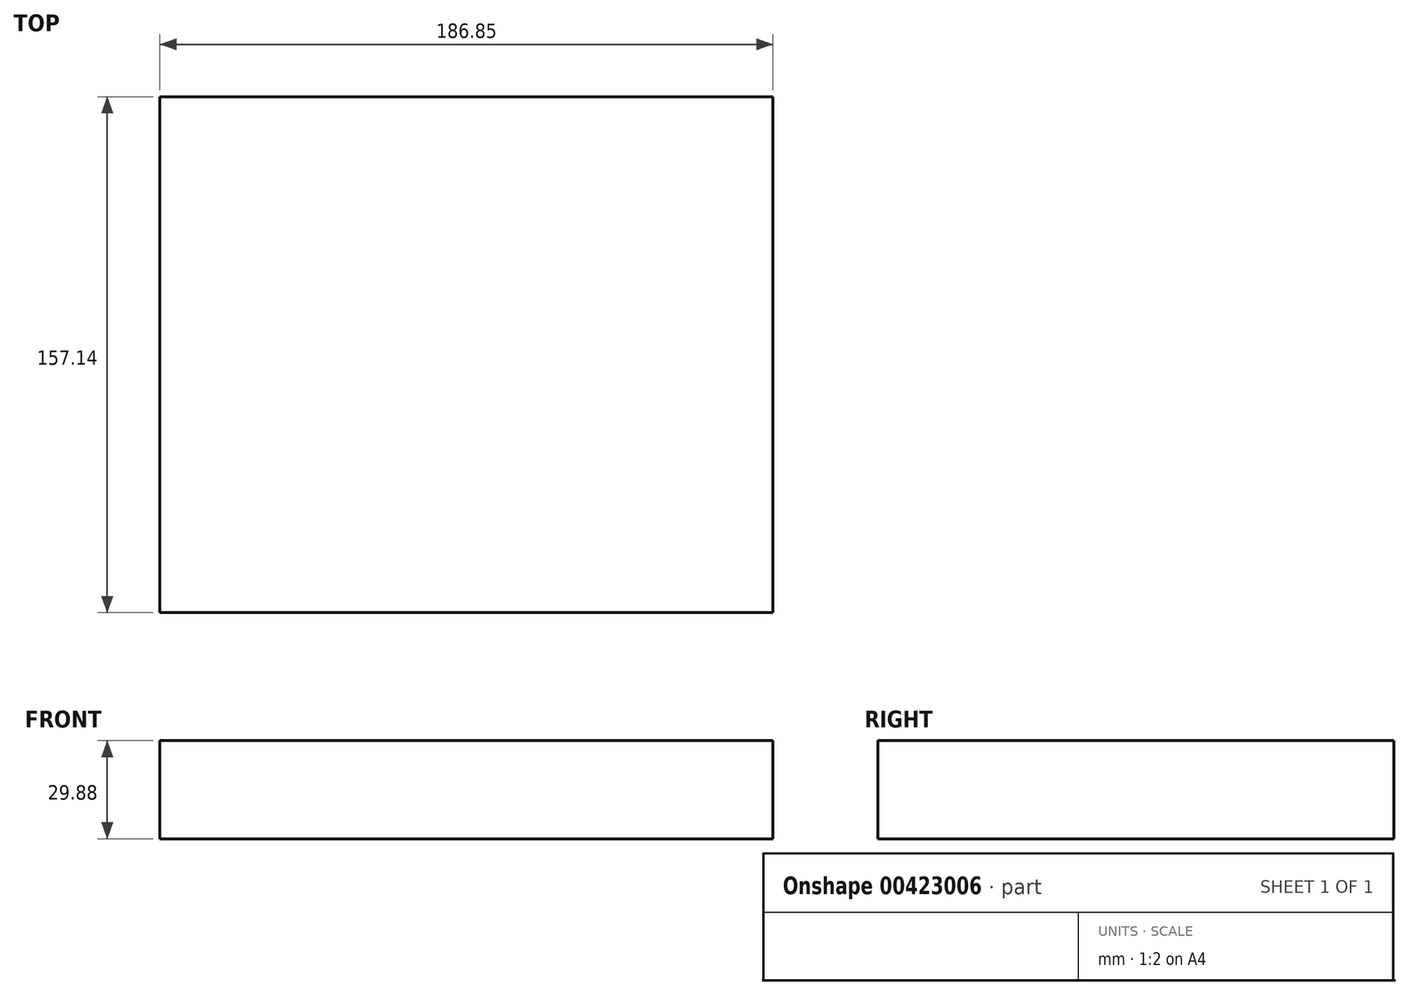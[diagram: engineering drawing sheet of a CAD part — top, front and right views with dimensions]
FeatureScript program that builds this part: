
annotation { "Feature Type Name" : "Feature", "Feature Type Description" : "" }
export const myFeature = defineFeature(function(context is Context, id is Id, definition is map)
    precondition{}
    {
        {
            var Q0;
            Q0=qCreatedBy(makeId("Front.planeOp"),FACE);
            var sketch = newSketch(context, id + "F0", { "sketchPlane" : qUnion([Q0])});
            skLineSegment(sketch, "E0.bottom", {"start": v(2281.78, 343.59) * mm, "end": v(2094.93, 343.59) * mm});
            skLineSegment(sketch, "E0.top", {"start": v(2281.78, 313.7) * mm, "end": v(2094.93, 313.7) * mm});
            skLineSegment(sketch, "E0.left", {"start": v(2281.78, 343.59) * mm, "end": v(2281.78, 313.7) * mm});
            skLineSegment(sketch, "E0.right", {"start": v(2094.93, 343.59) * mm, "end": v(2094.93, 313.7) * mm});
            skLineSegment(sketch, "E1.bottom", {"start": v(834.95, 135.04) * mm, "end": v(1410.14, 135.04) * mm});
            skLineSegment(sketch, "E1.top", {"start": v(834.95, 222.8) * mm, "end": v(1410.14, 222.8) * mm});
            skLineSegment(sketch, "E1.left", {"start": v(834.95, 135.04) * mm, "end": v(834.95, 222.8) * mm});
            skLineSegment(sketch, "E1.right", {"start": v(1410.14, 135.04) * mm, "end": v(1410.14, 222.8) * mm});
            skSolve(sketch);
        }
        {
            var Q0;
            Q0=makeQuery(id+"F0.imprint","IMPRINT",FACE,{"disambiguationData":[TD([[makeQuery(id+"F0.imprint","IMPRINT",EDGE,{"derivedFrom":sQuery(id+"F0.wireOp",EDGE,"E0.bottom")}),1.0]])]});
            extrude(context, id + "F1", {"entities" : qUnion([Q0]), "depth" : 157.14 * mm});
        }
    });
